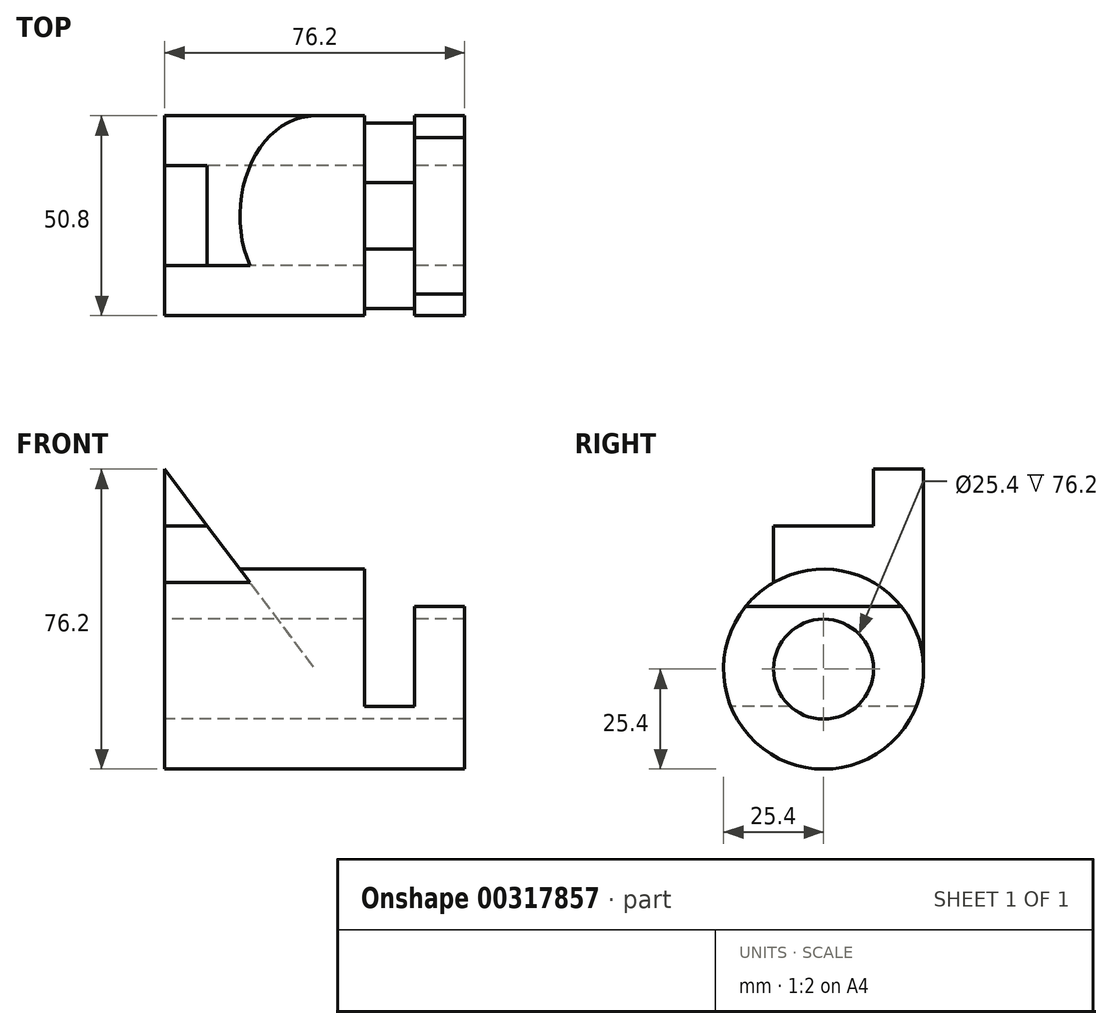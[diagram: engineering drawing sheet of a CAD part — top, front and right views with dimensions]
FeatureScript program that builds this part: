
annotation { "Feature Type Name" : "Feature", "Feature Type Description" : "" }
export const myFeature = defineFeature(function(context is Context, id is Id, definition is map)
    precondition{}
    {
        {
            var Q0;
            Q0=qCreatedBy(makeId("Right.planeOp"),FACE);
            var sketch = newSketch(context, id + "F0", { "sketchPlane" : qUnion([Q0])});
            skCircle(sketch, "E0", {"center": v(0, 0) * mm, "radius": 12.7 * mm});
            skCircle(sketch, "E1", {"center": v(0, 0) * mm, "radius": 25.4 * mm});
            skSolve(sketch);
        }
        {
            var Q0;
            Q0 = qSketchRegion(id + "F0", true);
            extrude(context, id + "F1", {"entities" : qUnion([Q0]), "depth" : 76.2 * mm});
        }
        {
            var Q0;
            Q0=qCreatedBy(makeId("Front.planeOp"),FACE);
            var sketch = newSketch(context, id + "F2", { "sketchPlane" : qUnion([Q0])});
            skLineSegment(sketch, "E2", {"start": v(0, 0) * mm, "end": v(0, 50.8) * mm});
            skLineSegment(sketch, "E3", {"start": v(0, 50.8) * mm, "end": v(38.1, 0) * mm});
            skLineSegment(sketch, "E4", {"start": v(38.1, 0) * mm, "end": v(0, 0) * mm});
            skLineSegment(sketch, "E5", {"start": v(0, 22.01) * mm, "end": v(21.59, 22.01) * mm});
            skSolve(sketch);
        }
        {
            var Q0;
            Q0 = qSketchRegion(id + "F2", true);
            extrude(context, id + "F3", {"entities" : qUnion([Q0]), "operationType" : NewBodyOperationType.ADD, "oppositeDirection" : true, "depth" : 25.4 * mm, "hasSecondDirection" : true, "secondDirectionOppositeDirection" : false, "secondDirectionDepth" : 12.7 * mm});
        }
        {
            var Q0;
            Q0=makeQuery(id+"F3.opExtrude","CAP_FACE",FACE,{"disambiguationData":[OSD([sQuery(id+"F2.wireOp",EDGE,"E2"),sQuery(id+"F2.wireOp",EDGE,"E3"),sQuery(id+"F2.wireOp",EDGE,"E4")])],"isStart":true});
            var sketch = newSketch(context, id + "F4", { "sketchPlane" : qUnion([Q0])});
            skLineSegment(sketch, "E6", {"start": v(0, 36.4) * mm, "end": v(10.8, 36.4) * mm});
            skLineSegment(sketch, "E7", {"start": v(10.8, 36.4) * mm, "end": v(0, 50.8) * mm});
            skLineSegment(sketch, "E8", {"start": v(0, 50.8) * mm, "end": v(0, 36.4) * mm});
            skSolve(sketch);
        }
        {
            var Q0;
            Q0 = qSketchRegion(id + "F4", true);
            extrude(context, id + "F5", {"entities" : qUnion([Q0]), "operationType" : NewBodyOperationType.REMOVE, "oppositeDirection" : true, "depth" : 25.4 * mm});
        }
        {
            var Q0;
            Q0=qCreatedBy(makeId("Right.planeOp"),FACE);
            var sketch = newSketch(context, id + "F6", { "sketchPlane" : qUnion([Q0])});
            skCircle(sketch, "E9", {"center": v(0, 0) * mm, "radius": 12.7 * mm});
            skSolve(sketch);
        }
        {
            var Q0;
            Q0 = qSketchRegion(id + "F6", true);
            extrude(context, id + "F7", {"entities" : qUnion([Q0]), "operationType" : NewBodyOperationType.REMOVE, "endBound" : BoundingType.THROUGH_ALL, "depth" : 25.4 * mm});
        }
        {
            var Q0;
            Q0=qCreatedBy(makeId("Front.planeOp"),FACE);
            var sketch = newSketch(context, id + "F8", { "sketchPlane" : qUnion([Q0])});
            skLineSegment(sketch, "E10", {"start": v(50.8, 25.4) * mm, "end": v(50.8, -9.52) * mm});
            skLineSegment(sketch, "E11", {"start": v(50.8, -9.52) * mm, "end": v(63.5, -9.52) * mm});
            skLineSegment(sketch, "E12", {"start": v(63.5, -9.52) * mm, "end": v(63.5, 15.88) * mm});
            skLineSegment(sketch, "E13", {"start": v(63.5, 15.88) * mm, "end": v(76.2, 15.88) * mm});
            skLineSegment(sketch, "E14", {"start": v(76.2, 15.88) * mm, "end": v(76.2, 25.4) * mm});
            skLineSegment(sketch, "E15", {"start": v(76.2, 25.4) * mm, "end": v(50.8, 25.4) * mm});
            skSolve(sketch);
        }
        {
            var Q0;
            Q0 = qSketchRegion(id + "F8", true);
            extrude(context, id + "F9", {"entities" : qUnion([Q0]), "operationType" : NewBodyOperationType.REMOVE, "endBound" : BoundingType.THROUGH_ALL, "oppositeDirection" : true, "depth" : 25.4 * mm, "hasSecondDirection" : true, "secondDirectionOppositeDirection" : false, "secondDirectionDepth" : 25.4 * mm});
        }
    });
